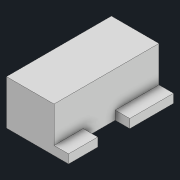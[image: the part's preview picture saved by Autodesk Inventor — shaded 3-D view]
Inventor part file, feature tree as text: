
AUTODESK INVENTOR PART (.ipt)
format: ipt  version: 2022 (Build 260153000, 153)  size: 97,792 bytes
history: native  units: mm
features: extrude x2, sketch x2
ambient origin geometry x8: Origin, YZ Plane, XZ Plane, XY Plane, X Axis, Y Axis, Z Axis, Center Point
bodies: Solid1 (feature_tree)
feature tree (4):
  extrude  "Extrusion1"  Depth=16.3mm
  extrude  "Extrusion2"  Depth=10.0mm
  sketch  "Sketch1"  dims[d0=36.0mm d1=16.3mm]
  sketch  "Sketch2"  dims[d2=15.3mm d3=0.0mm d4=10.0mm d5=3.0mm d6=15.0mm d7=5.0mm d8=0.0mm]
